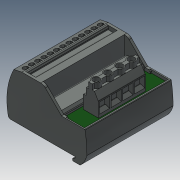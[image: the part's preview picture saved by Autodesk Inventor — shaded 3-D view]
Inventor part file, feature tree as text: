
AUTODESK INVENTOR PART (.ipt)
format: ipt  version: 2018.3 (Build 223284000, 284)  size: 551,936 bytes
history: native  units: in
note: dims shown in document units (in); Inventor stores cm internally (conversion verified against a paired STEP export)
features: plane x2
ambient origin geometry x8: Origin, YZ Plane, XZ Plane, XY Plane, X Axis, Y Axis, Z Axis, Center Point
bodies: Solid1 (feature_tree)
feature tree (2):
  plane  "Work Plane1"
  plane  "Work Plane2"
